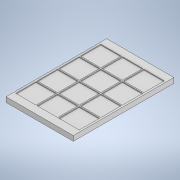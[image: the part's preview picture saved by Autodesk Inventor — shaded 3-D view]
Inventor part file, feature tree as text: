
AUTODESK INVENTOR PART (.ipt)
format: ipt  version: 2020 (Build 240168000, 168)  size: 148,480 bytes
history: native  units: in
note: dims shown in document units (in); Inventor stores cm internally (conversion verified against a paired STEP export)
features: extrude x2, sketch x2, pattern_linear x1
ambient origin geometry x8: Origin, YZ Plane, XZ Plane, XY Plane, X Axis, Y Axis, Z Axis, Center Point
bodies: Solid1 (feature_tree)
feature tree (5):
  extrude  "Extrusion1"  Depth=5.0299in
  extrude  "Extrusion2"  Depth=1.0787in
  pattern_linear  "Rectangular Pattern2"  Spacing1=0.25in  [1 undecoded]
  sketch  "Sketch1"  dims[d0=3.3654in d1=5.0299in]
  sketch  "Sketch3"  dims[d3=45.0deg d4=0.375in d5=0.25in d6=0.0in d23=0.094in d24=0.387in d25=1.0197in d26=1.0197in d27=0.0394in d28=0.0394in d29=0.0394in d30=0.0in d31=1.1811in d33=1.0787in d34=1.5748in d36=1.0787in]
note: 1 required parameter value undecoded (feature->parameter linkage not recoverable at this tier; creation-order binding heuristic only, values carry confidence <= 0.55)
